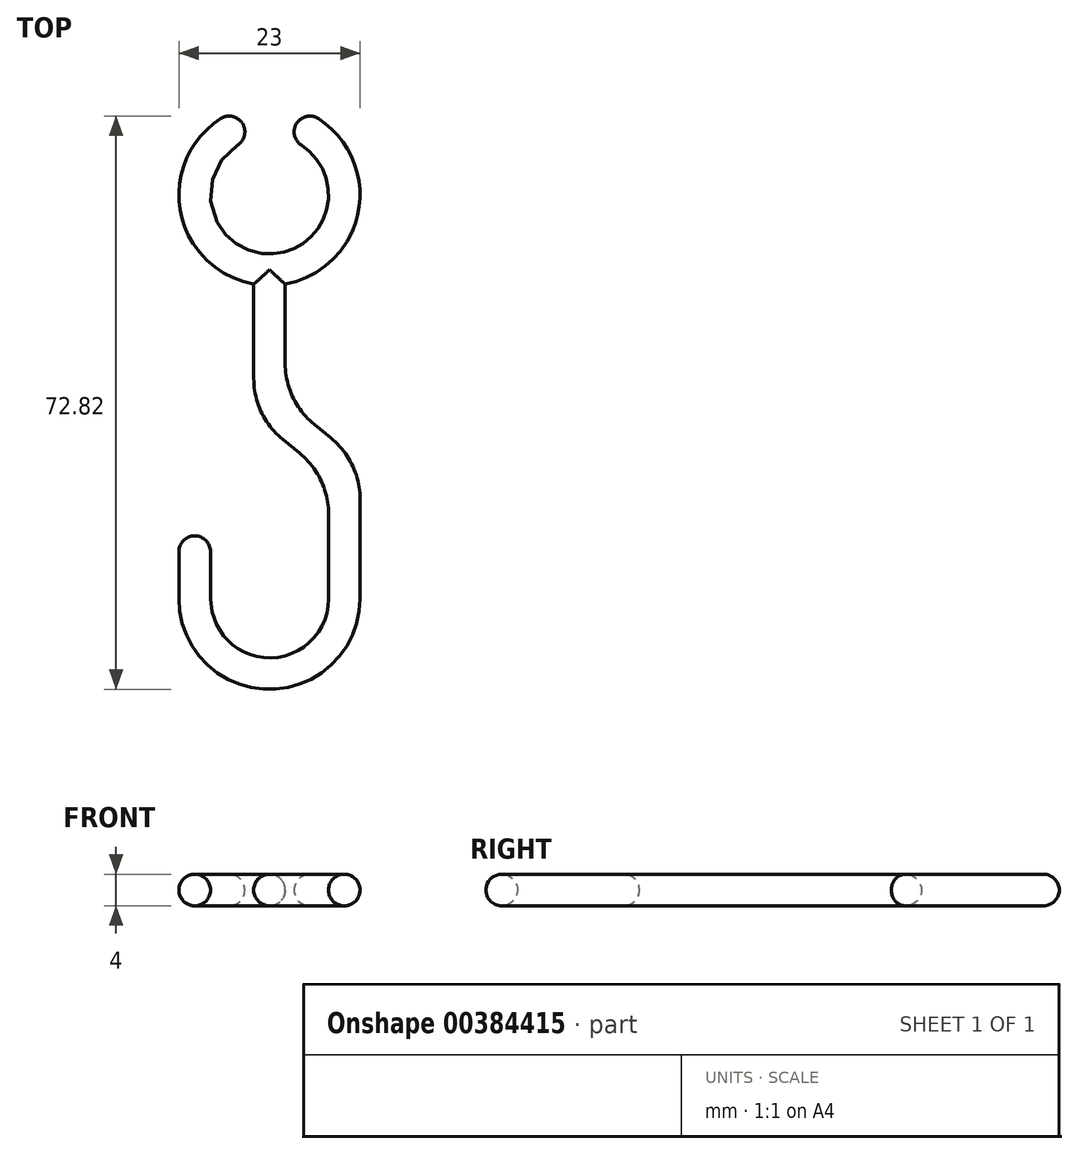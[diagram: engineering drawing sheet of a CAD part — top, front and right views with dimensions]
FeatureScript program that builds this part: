
annotation { "Feature Type Name" : "Feature", "Feature Type Description" : "" }
export const myFeature = defineFeature(function(context is Context, id is Id, definition is map)
    precondition{}
    {
        {
            var Q0;
            Q0=qCreatedBy(makeId("Top.planeOp"),FACE);
            var sketch = newSketch(context, id + "F0", { "sketchPlane" : qUnion([Q0])});
            skArc(sketch, "E0", {"start": v(-4.05, 6.31) * mm, "mid": v(0, -7.5) * mm, "end": v(4.05, 6.31) * mm});
            skArc(sketch, "E1.0", {"start": v(-6.2, 9.68) * mm, "mid": v(-11.28, -2.26) * mm, "end": v(-2, -11.32) * mm});
            skLineSegment(sketch, "E2.left", {"start": v(2, -11.32) * mm, "end": v(2, -21.42) * mm});
            skLineSegment(sketch, "E2.right", {"start": v(-2, -11.32) * mm, "end": v(-2, -23.32) * mm});
            skLineSegment(sketch, "E3", {"start": v(11.5, -25.5) * mm, "end": v(11.5, -65.48) * mm, "construction": true});
            skLineSegment(sketch, "E4.left", {"start": v(11.5, -38.65) * mm, "end": v(11.5, -51.32) * mm});
            skLineSegment(sketch, "E4.right", {"start": v(7.5, -40.56) * mm, "end": v(7.5, -51.32) * mm});
            skLineSegment(sketch, "E5", {"start": v(1.7, -31.1) * mm, "end": v(3.8, -32.8) * mm});
            skLineSegment(sketch, "E6", {"start": v(5.7, -29.19) * mm, "end": v(7.8, -30.88) * mm});
            skArc(sketch, "E7.filletArc", {"start": v(2, -21.42) * mm, "mid": v(2.97, -25.72) * mm, "end": v(5.7, -29.19) * mm});
            skArc(sketch, "E8.filletArc", {"start": v(-2, -23.32) * mm, "mid": v(-1.03, -27.63) * mm, "end": v(1.7, -31.1) * mm});
            skArc(sketch, "E9.filletArc", {"start": v(7.5, -40.56) * mm, "mid": v(6.53, -36.26) * mm, "end": v(3.8, -32.8) * mm});
            skArc(sketch, "E10.filletArc", {"start": v(11.5, -38.65) * mm, "mid": v(10.53, -34.35) * mm, "end": v(7.8, -30.88) * mm});
            skArc(sketch, "E11", {"start": v(-7.5, -51.32) * mm, "mid": v(0, -58.82) * mm, "end": v(7.5, -51.32) * mm});
            skArc(sketch, "E12.0", {"start": v(-11.5, -51.32) * mm, "mid": v(0, -62.82) * mm, "end": v(11.5, -51.32) * mm});
            skLineSegment(sketch, "E13.left", {"start": v(-11.5, -51.32) * mm, "end": v(-11.5, -51.32) * mm});
            skLineSegment(sketch, "E13.right", {"start": v(-7.5, -51.32) * mm, "end": v(-7.5, -51.32) * mm});
            skLineSegment(sketch, "E14.top", {"start": v(-9.5, -43.32) * mm, "end": v(-9.5, -43.32) * mm});
            skLineSegment(sketch, "E14.left", {"start": v(-11.5, -51.32) * mm, "end": v(-11.5, -45.32) * mm});
            skLineSegment(sketch, "E14.right", {"start": v(-7.5, -51.32) * mm, "end": v(-7.5, -45.32) * mm});
            skPoint(sketch, "E15.visualSharp", {"position": v(-7.5, -43.32) * mm});
            skArc(sketch, "E15.filletArc", {"start": v(-7.5, -45.32) * mm, "mid": v(-8.09, -43.91) * mm, "end": v(-9.5, -43.32) * mm});
            skPoint(sketch, "E16.visualSharp", {"position": v(-11.5, -43.32) * mm});
            skArc(sketch, "E16.filletArc", {"start": v(-9.5, -43.32) * mm, "mid": v(-10.91, -43.91) * mm, "end": v(-11.5, -45.32) * mm});
            skLineSegment(sketch, "E17", {"start": v(0, 0) * mm, "end": v(0, 14) * mm, "construction": true});
            skPoint(sketch, "E18", {"position": v(2.5, 7.07) * mm});
            skPoint(sketch, "E19.MirrorP", {"position": v(-2.5, 7.07) * mm});
            skLineSegment(sketch, "E20", {"start": v(-3.31, 8.83) * mm, "end": v(-3.31, 8.83) * mm});
            skLineSegment(sketch, "E21", {"start": v(-4.18, 10.71) * mm, "end": v(0.24, 12.44) * mm, "construction": true});
            skLineSegment(sketch, "E22.MirrorCS", {"start": v(3.31, 8.83) * mm, "end": v(3.31, 8.83) * mm});
            skPoint(sketch, "E23.visualSharp", {"position": v(-4.18, 10.71) * mm});
            skArc(sketch, "E23.filletArc", {"start": v(-3.31, 8.83) * mm, "mid": v(-4.57, 9.92) * mm, "end": v(-6.2, 9.68) * mm});
            skArc(sketch, "E24.filletArc", {"start": v(-4.05, 6.31) * mm, "mid": v(-3.2, 7.44) * mm, "end": v(-3.31, 8.83) * mm});
            skArc(sketch, "E25.filletArc", {"start": v(3.31, 8.83) * mm, "mid": v(3.2, 7.44) * mm, "end": v(4.05, 6.31) * mm});
            skPoint(sketch, "E26.visualSharp", {"position": v(4.18, 10.71) * mm});
            skArc(sketch, "E26.filletArc", {"start": v(6.2, 9.68) * mm, "mid": v(4.57, 9.92) * mm, "end": v(3.31, 8.83) * mm});
            skArc(sketch, "E27.trimOffspring", {"start": v(2, -11.32) * mm, "mid": v(11.28, -2.26) * mm, "end": v(6.2, 9.68) * mm});
            skSolve(sketch);
        }
        {
            var Q0;
            Q0=makeQuery(id+"F0.imprint","IMPRINT",FACE,{"disambiguationData":[TD([[makeQuery(id+"F0.imprint","IMPRINT",EDGE,{"derivedFrom":sQuery(id+"F0.wireOp",EDGE,"E0")}),-1.0]])]});
            extrude(context, id + "F1", {"entities" : qUnion([Q0]), "depth" : 4 * mm});
        }
        {
            var Q0;
            Q0=makeQuery(id+"F1.opExtrude","CAP_FACE",FACE,{"disambiguationData":[OSD([sQuery(id+"F0.wireOp",EDGE,"E0"),sQuery(id+"F0.wireOp",EDGE,"E1.0"),sQuery(id+"F0.wireOp",EDGE,"E2.left"),sQuery(id+"F0.wireOp",EDGE,"E2.right"),sQuery(id+"F0.wireOp",EDGE,"E4.left"),sQuery(id+"F0.wireOp",EDGE,"E4.right"),sQuery(id+"F0.wireOp",EDGE,"E5"),sQuery(id+"F0.wireOp",EDGE,"E6"),sQuery(id+"F0.wireOp",EDGE,"E7.filletArc"),sQuery(id+"F0.wireOp",EDGE,"E8.filletArc"),sQuery(id+"F0.wireOp",EDGE,"E9.filletArc"),sQuery(id+"F0.wireOp",EDGE,"E10.filletArc"),sQuery(id+"F0.wireOp",EDGE,"E11"),sQuery(id+"F0.wireOp",EDGE,"E12.0"),sQuery(id+"F0.wireOp",EDGE,"E14.left"),sQuery(id+"F0.wireOp",EDGE,"E14.right"),sQuery(id+"F0.wireOp",EDGE,"E15.filletArc"),sQuery(id+"F0.wireOp",EDGE,"E16.filletArc"),sQuery(id+"F0.wireOp",EDGE,"E23.filletArc"),sQuery(id+"F0.wireOp",EDGE,"E24.filletArc"),sQuery(id+"F0.wireOp",EDGE,"E25.filletArc"),sQuery(id+"F0.wireOp",EDGE,"E26.filletArc"),sQuery(id+"F0.wireOp",EDGE,"E27.trimOffspring")])],"isStart":false});
            var Q1;
            Q1=makeQuery(id+"F1.opExtrude","CAP_FACE",FACE,{"disambiguationData":[OSD([sQuery(id+"F0.wireOp",EDGE,"E0"),sQuery(id+"F0.wireOp",EDGE,"E1.0"),sQuery(id+"F0.wireOp",EDGE,"E2.left"),sQuery(id+"F0.wireOp",EDGE,"E2.right"),sQuery(id+"F0.wireOp",EDGE,"E4.left"),sQuery(id+"F0.wireOp",EDGE,"E4.right"),sQuery(id+"F0.wireOp",EDGE,"E5"),sQuery(id+"F0.wireOp",EDGE,"E6"),sQuery(id+"F0.wireOp",EDGE,"E7.filletArc"),sQuery(id+"F0.wireOp",EDGE,"E8.filletArc"),sQuery(id+"F0.wireOp",EDGE,"E9.filletArc"),sQuery(id+"F0.wireOp",EDGE,"E10.filletArc"),sQuery(id+"F0.wireOp",EDGE,"E11"),sQuery(id+"F0.wireOp",EDGE,"E12.0"),sQuery(id+"F0.wireOp",EDGE,"E14.left"),sQuery(id+"F0.wireOp",EDGE,"E14.right"),sQuery(id+"F0.wireOp",EDGE,"E15.filletArc"),sQuery(id+"F0.wireOp",EDGE,"E16.filletArc"),sQuery(id+"F0.wireOp",EDGE,"E23.filletArc"),sQuery(id+"F0.wireOp",EDGE,"E24.filletArc"),sQuery(id+"F0.wireOp",EDGE,"E25.filletArc"),sQuery(id+"F0.wireOp",EDGE,"E26.filletArc"),sQuery(id+"F0.wireOp",EDGE,"E27.trimOffspring")])],"isStart":true});
            fillet(context, id + "F2", {"entities" : qUnion([Q0, Q1]), "radius" : 2 * mm, "tangentPropagation" : true, "allowEdgeOverflow" : false});
        }
    });
